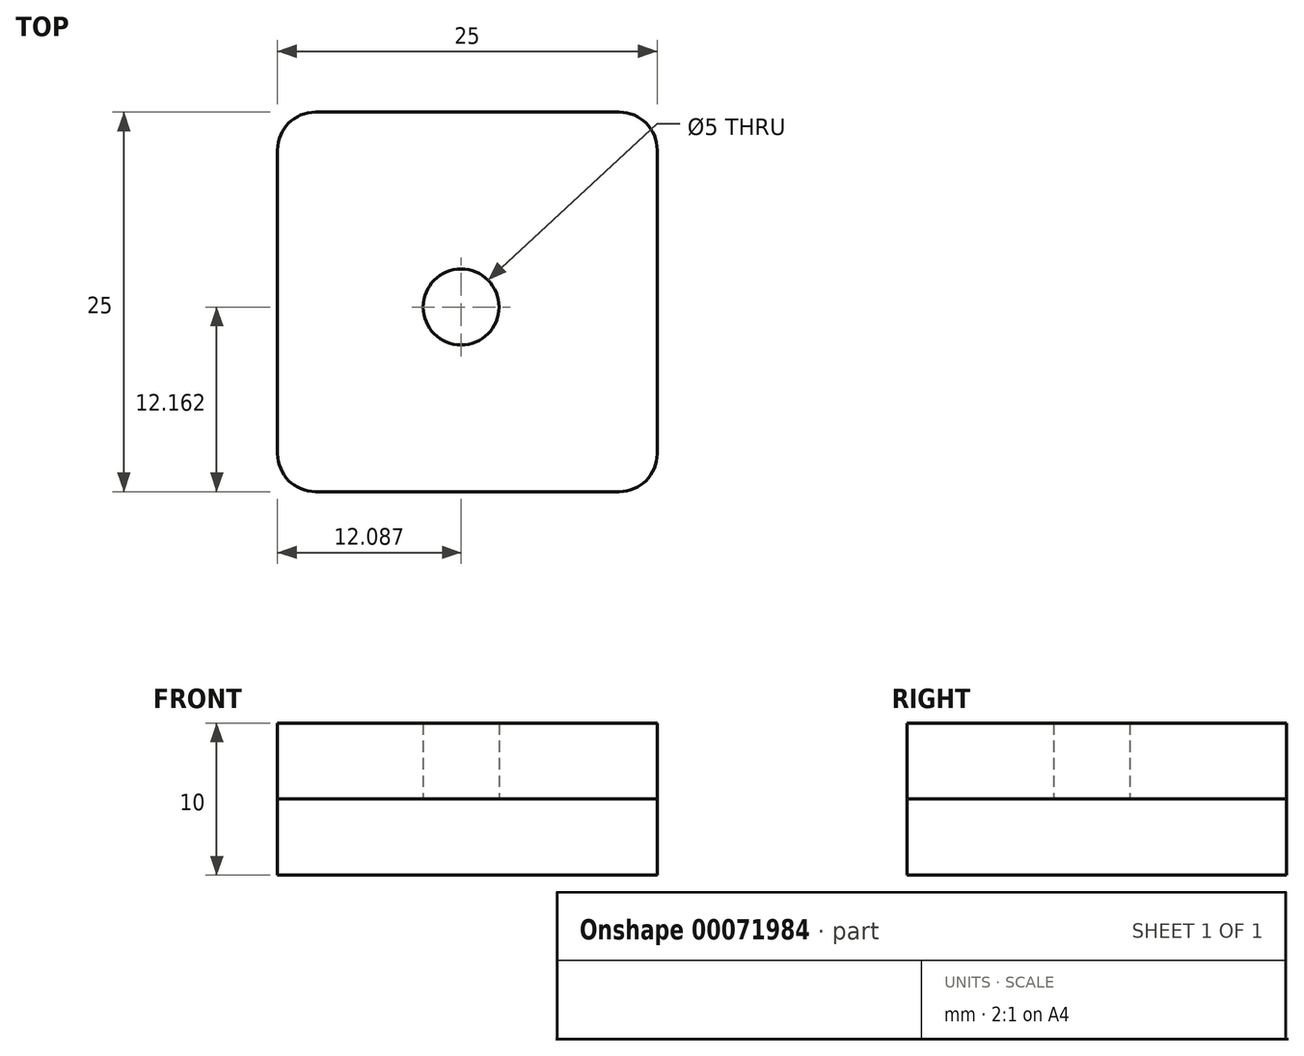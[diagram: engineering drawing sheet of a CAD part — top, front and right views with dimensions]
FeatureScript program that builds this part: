
annotation { "Feature Type Name" : "Feature", "Feature Type Description" : "" }
export const myFeature = defineFeature(function(context is Context, id is Id, definition is map)
    precondition{}
    {
        {
            var Q0;
            Q0=qCreatedBy(makeId("Top.planeOp"),FACE);
            var sketch = newSketch(context, id + "F0", { "sketchPlane" : qUnion([Q0])});
            skLineSegment(sketch, "E0.bottom", {"start": v(-20.44, 6.02) * mm, "end": v(-0.44, 6.02) * mm});
            skLineSegment(sketch, "E0.top", {"start": v(-20.44, -18.98) * mm, "end": v(-0.44, -18.98) * mm});
            skLineSegment(sketch, "E0.left", {"start": v(-22.94, 3.52) * mm, "end": v(-22.94, -16.48) * mm});
            skLineSegment(sketch, "E0.right", {"start": v(2.06, 3.52) * mm, "end": v(2.06, -16.48) * mm});
            skPoint(sketch, "E1.visualSharp", {"position": v(-22.94, 6.02) * mm});
            skArc(sketch, "E1.filletArc", {"start": v(-20.44, 6.02) * mm, "mid": v(-22.2, 5.29) * mm, "end": v(-22.94, 3.52) * mm});
            skPoint(sketch, "E2.visualSharp", {"position": v(2.06, 6.02) * mm});
            skArc(sketch, "E2.filletArc", {"start": v(2.06, 3.52) * mm, "mid": v(1.33, 5.29) * mm, "end": v(-0.44, 6.02) * mm});
            skPoint(sketch, "E3.visualSharp", {"position": v(2.06, -18.98) * mm});
            skArc(sketch, "E3.filletArc", {"start": v(-0.44, -18.98) * mm, "mid": v(1.33, -18.25) * mm, "end": v(2.06, -16.48) * mm});
            skPoint(sketch, "E4.visualSharp", {"position": v(-22.94, -18.98) * mm});
            skArc(sketch, "E4.filletArc", {"start": v(-22.94, -16.48) * mm, "mid": v(-22.2, -18.25) * mm, "end": v(-20.44, -18.98) * mm});
            skCircle(sketch, "E5", {"center": v(-10.85, -6.82) * mm, "radius": 2.5 * mm});
            skSolve(sketch);
        }
        {
            var Q0;
            Q0 = qSketchRegion(id + "F0", true);
            extrude(context, id + "F1", {"entities" : qUnion([Q0]), "depth" : 5 * mm});
        }
        {
            var Q0;
            Q0=makeQuery(id+"F0.imprint","IMPRINT",FACE,{"disambiguationData":[TD([[makeQuery(id+"F0.imprint","IMPRINT",EDGE,{"derivedFrom":sQuery(id+"F0.wireOp",EDGE,"E0.bottom")}),-1.0]])]});
            var Q1;
            Q1=makeQuery(id+"F0.imprint","IMPRINT",FACE,{"disambiguationData":[TD([[makeQuery(id+"F0.imprint","IMPRINT",EDGE,{"derivedFrom":sQuery(id+"F0.wireOp",EDGE,"E5")}),1.0]])]});
            extrude(context, id + "F2", {"entities" : qUnion([Q0, Q1]), "oppositeDirection" : true, "depth" : 5 * mm});
        }
    });
